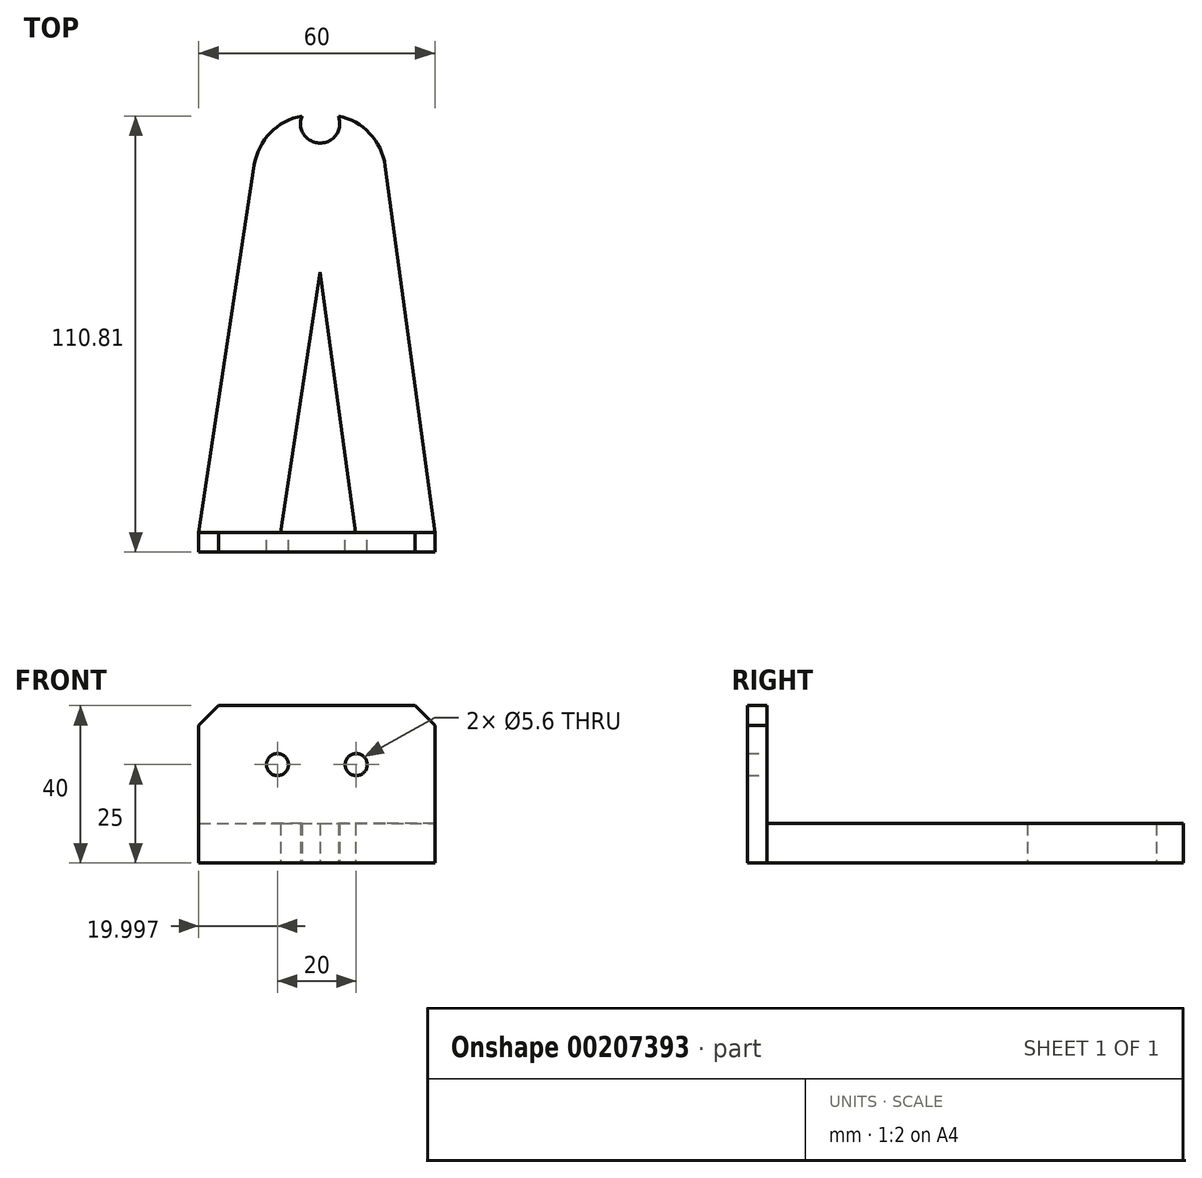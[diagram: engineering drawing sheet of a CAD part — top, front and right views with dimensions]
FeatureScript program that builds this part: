
annotation { "Feature Type Name" : "Feature", "Feature Type Description" : "" }
export const myFeature = defineFeature(function(context is Context, id is Id, definition is map)
    precondition{}
    {
        {
            var Q0;
            Q0=qCreatedBy(makeId("Top.planeOp"),FACE);
            var sketch = newSketch(context, id + "F0", { "sketchPlane" : qUnion([Q0])});
            skLineSegment(sketch, "E0.bottom", {"start": v(-59.78, -71.73) * mm, "end": v(0.22, -71.73) * mm});
            skLineSegment(sketch, "E0.top", {"start": v(-59.78, -76.73) * mm, "end": v(0.22, -76.73) * mm});
            skLineSegment(sketch, "E0.left", {"start": v(-59.78, -71.73) * mm, "end": v(-59.78, -76.73) * mm});
            skLineSegment(sketch, "E0.right", {"start": v(0.22, -71.73) * mm, "end": v(0.22, -76.73) * mm});
            skLineSegment(sketch, "E1", {"start": v(-59.78, -71.73) * mm, "end": v(-43.55, 35.59) * mm});
            skLineSegment(sketch, "E2", {"start": v(0.22, -71.73) * mm, "end": v(-14.34, 35.48) * mm});
            skLineSegment(sketch, "E3", {"start": v(-38.96, -71.73) * mm, "end": v(-28.95, -5.54) * mm});
            skLineSegment(sketch, "E4", {"start": v(-28.95, -5.54) * mm, "end": v(-19.97, -71.73) * mm});
            skPoint(sketch, "E5", {"position": v(-29.78, -76.73) * mm});
            skLineSegment(sketch, "E6", {"start": v(-43.55, 35.59) * mm, "end": v(-33.58, 34.08) * mm});
            skLineSegment(sketch, "E7", {"start": v(-14.34, 35.48) * mm, "end": v(-24.33, 34.08) * mm});
            skArc(sketch, "E8", {"start": v(-33.58, 34.08) * mm, "mid": v(-28.95, 27.17) * mm, "end": v(-24.33, 34.08) * mm});
            skSolve(sketch);
        }
        {
            var Q0;
            {var subQ2=sQuery(id+"F0.wireOp",EDGE,"E1");Q0=makeQuery(id+"F0.imprint","IMPRINT",FACE,{"disambiguationData":[TD([[makeQuery(id+"F0.imprint","IMPRINT",EDGE,{"derivedFrom":subQ2}),-1.0]])]});}
            extrude(context, id + "F1", {"entities" : qUnion([Q0]), "depth" : 10 * mm});
        }
        {
            var Q0;
            Q0=makeQuery(id+"F0.imprint","IMPRINT",FACE,{"disambiguationData":[TD([[makeQuery(id+"F0.imprint","IMPRINT",EDGE,{"derivedFrom":sQuery(id+"F0.wireOp",EDGE,"E0.top")}),1.0]])]});
            extrude(context, id + "F2", {"entities" : qUnion([Q0]), "operationType" : NewBodyOperationType.ADD, "depth" : 40 * mm});
        }
        {
            var Q0;
            Q0=makeQuery(id+"F2.opExtrude","SWEPT_FACE",FACE,{"disambiguationData":[OSD([sQuery(id+"F0.wireOp",EDGE,"E0.bottom")])]});
            var sketch = newSketch(context, id + "F3", { "sketchPlane" : qUnion([Q0])});
            skPoint(sketch, "E9", {"position": v(-0.22, 10) * mm});
            skLineSegment(sketch, "E10", {"start": v(-0.22, 10) * mm, "end": v(-0.22, 40) * mm, "construction": true});
            skPoint(sketch, "E11", {"position": v(-0.22, 25) * mm});
            skCircle(sketch, "E12", {"center": v(19.78, 25) * mm, "radius": 2.8 * mm});
            skCircle(sketch, "E13", {"center": v(39.78, 25) * mm, "radius": 2.8 * mm});
            skLineSegment(sketch, "E14", {"start": v(39.78, 25) * mm, "end": v(19.78, 25) * mm, "construction": true});
            skPoint(sketch, "E15", {"position": v(29.78, 25) * mm});
            skPoint(sketch, "E16", {"position": v(29.78, 40) * mm});
            skSolve(sketch);
        }
        {
            var Q0;
            Q0=makeQuery(id+"F3.imprint","IMPRINT",FACE,{"disambiguationData":[TD([[makeQuery(id+"F3.imprint","IMPRINT",EDGE,{"derivedFrom":sQuery(id+"F3.wireOp",EDGE,"E13")}),1.0]])]});
            var Q1;
            Q1=makeQuery(id+"F3.imprint","IMPRINT",FACE,{"disambiguationData":[TD([[makeQuery(id+"F3.imprint","IMPRINT",EDGE,{"derivedFrom":sQuery(id+"F3.wireOp",EDGE,"E12")}),1.0]])]});
            var Q2;
            Q2=makeQuery(id+"F2.opExtrude","SWEPT_FACE",FACE,{"disambiguationData":[OSD([sQuery(id+"F0.wireOp",EDGE,"E0.top")])]});
            extrude(context, id + "F4", {"entities" : qUnion([Q0, Q1]), "operationType" : NewBodyOperationType.REMOVE, "endBound" : BoundingType.UP_TO_SURFACE, "oppositeDirection" : true, "endBoundEntityFace" : qUnion([Q2]), "depth" : 25 * mm});
        }
        {
            var Q0;
            Q0=makeQuery(id+"F1.opExtrude","SWEPT_EDGE",EDGE,{"disambiguationData":[OSD([sQuery(id+"F0.wireOp",EDGE,"E1"),sQuery(id+"F0.wireOp",EDGE,"E6")])]});
            var Q1;
            Q1=makeQuery(id+"F1.opExtrude","SWEPT_EDGE",EDGE,{"disambiguationData":[OSD([sQuery(id+"F0.wireOp",EDGE,"E2"),sQuery(id+"F0.wireOp",EDGE,"E7")])]});
            fillet(context, id + "F5", {"entities" : qUnion([Q0, Q1]), "radius" : 15 * mm, "tangentPropagation" : true, "allowEdgeOverflow" : false});
        }
        {
            var Q0;
            Q0=makeQuery(id+"F2.opExtrude","CAP_EDGE",EDGE,{"disambiguationData":[OSD([sQuery(id+"F0.wireOp",EDGE,"E0.right")])],"isStart":false});
            var Q1;
            Q1=makeQuery(id+"F2.opExtrude","CAP_EDGE",EDGE,{"disambiguationData":[OSD([sQuery(id+"F0.wireOp",EDGE,"E0.left")])],"isStart":false});
            chamfer(context, id + "F6", {"entities" : qUnion([Q0, Q1]), "width" : 5 * mm, "tangentPropagation" : true});
        }
    });
